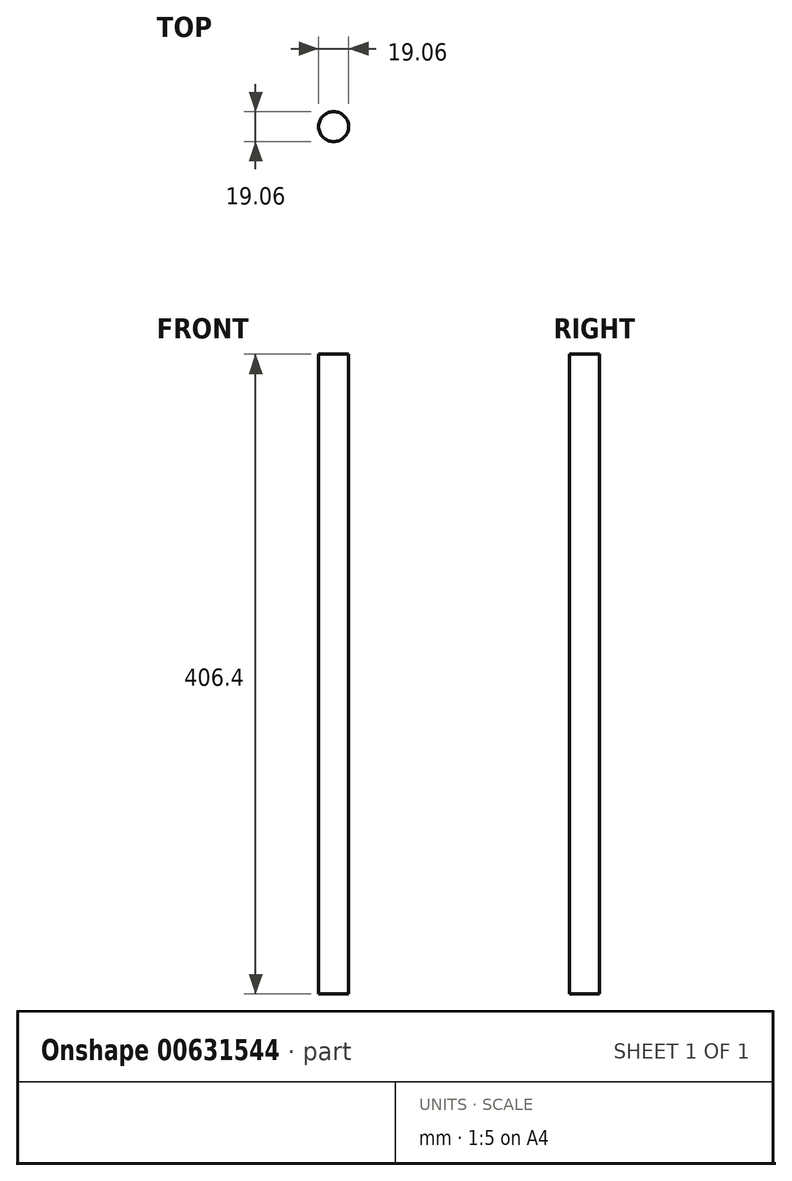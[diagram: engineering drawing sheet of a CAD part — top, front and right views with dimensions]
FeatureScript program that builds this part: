
annotation { "Feature Type Name" : "Feature", "Feature Type Description" : "" }
export const myFeature = defineFeature(function(context is Context, id is Id, definition is map)
    precondition{}
    {
        {
            var Q0;
            Q0=qCreatedBy(makeId("Top.planeOp"),FACE);
            var sketch = newSketch(context, id + "F0", { "sketchPlane" : qUnion([Q0])});
            skCircle(sketch, "E0", {"center": v(0, 0) * mm, "radius": 9.53 * mm});
            skSolve(sketch);
        }
        {
            var Q0;
            Q0=qSketchRegion(id+"F0",true);
            extrude(context, id + "F1", {"entities" : qUnion([Q0]), "depth" : 406.4 * mm, "offsetDistance" : 25.4 * mm});
        }
    });
